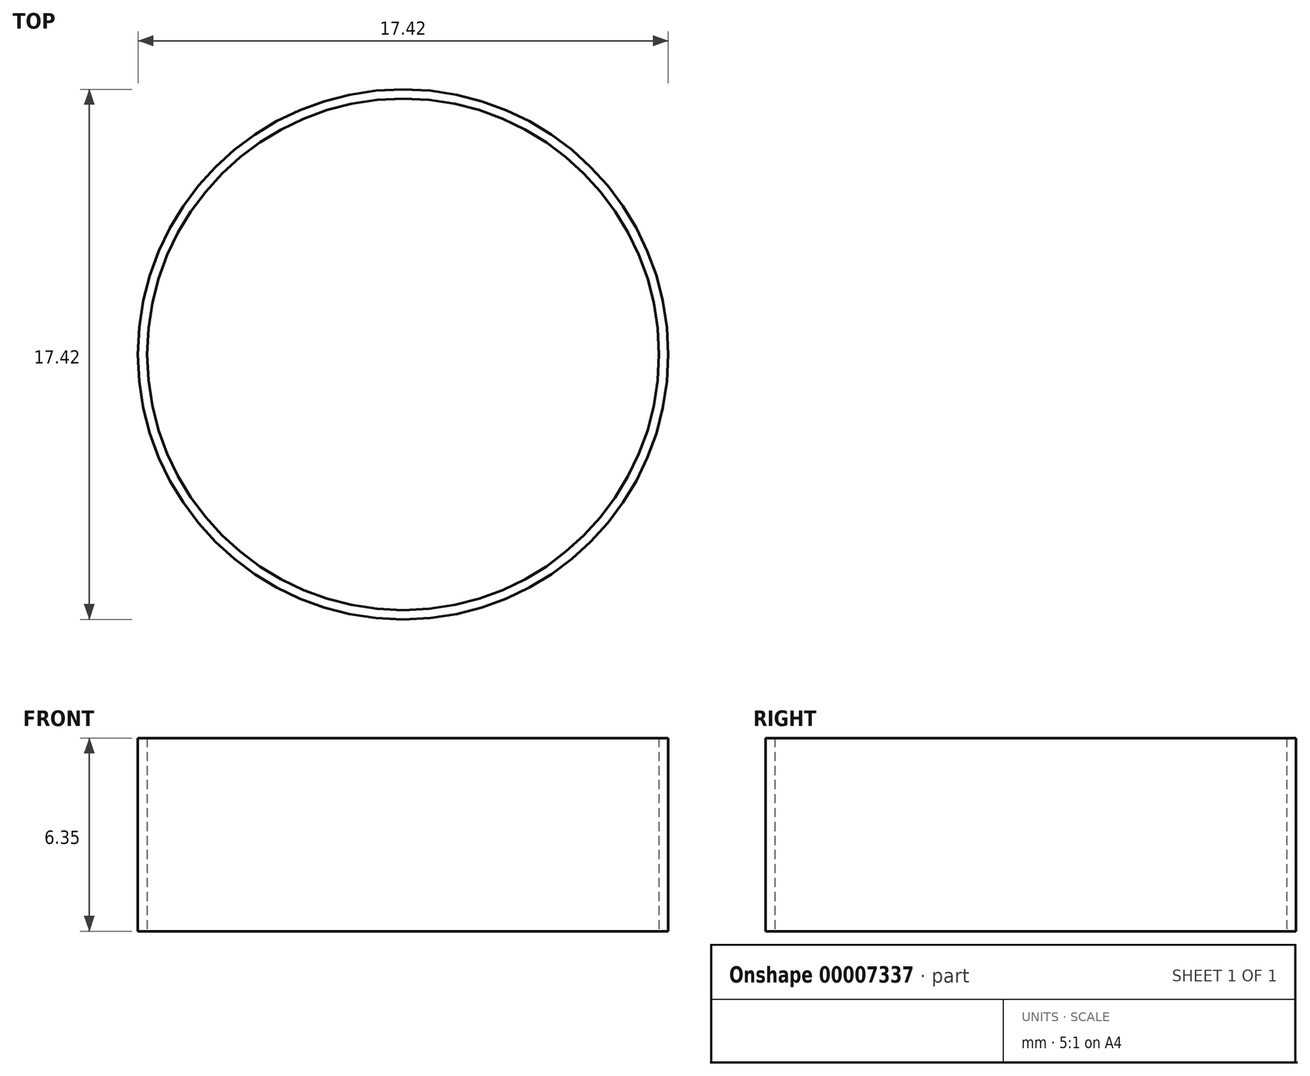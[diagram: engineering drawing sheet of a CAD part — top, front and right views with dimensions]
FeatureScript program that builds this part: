
annotation { "Feature Type Name" : "Feature", "Feature Type Description" : "" }
export const myFeature = defineFeature(function(context is Context, id is Id, definition is map)
    precondition{}
    {
        {
            var Q0;
            Q0=qCreatedBy(makeId("Front.planeOp"),FACE);
            var sketch = newSketch(context, id + "F0", { "sketchPlane" : qUnion([Q0])});
            skLineSegment(sketch, "E0.bottom", {"start": v(8.4, 0) * mm, "end": v(8.71, 0) * mm});
            skLineSegment(sketch, "E0.top", {"start": v(8.4, 6.35) * mm, "end": v(8.71, 6.35) * mm});
            skLineSegment(sketch, "E0.left", {"start": v(8.4, 0) * mm, "end": v(8.4, 6.35) * mm});
            skLineSegment(sketch, "E0.right", {"start": v(8.71, 0) * mm, "end": v(8.71, 6.35) * mm});
            skLineSegment(sketch, "E1", {"start": v(8.4, 0) * mm, "end": v(0, 0) * mm});
            skLineSegment(sketch, "E2", {"start": v(0, 0) * mm, "end": v(0, 6.35) * mm});
            skSolve(sketch);
        }
        {
            var Q0;
            Q0 = qSketchRegion(id + "F0", true);
            var Q1;
            Q1=sQuery(id+"F0.wireOp",EDGE,"E2");
            revolve(context, id + "F1", {"entities" : qUnion([Q0]), "axis" : qUnion([Q1]), "revolveType" : RevolveType.FULL});
        }
    });
